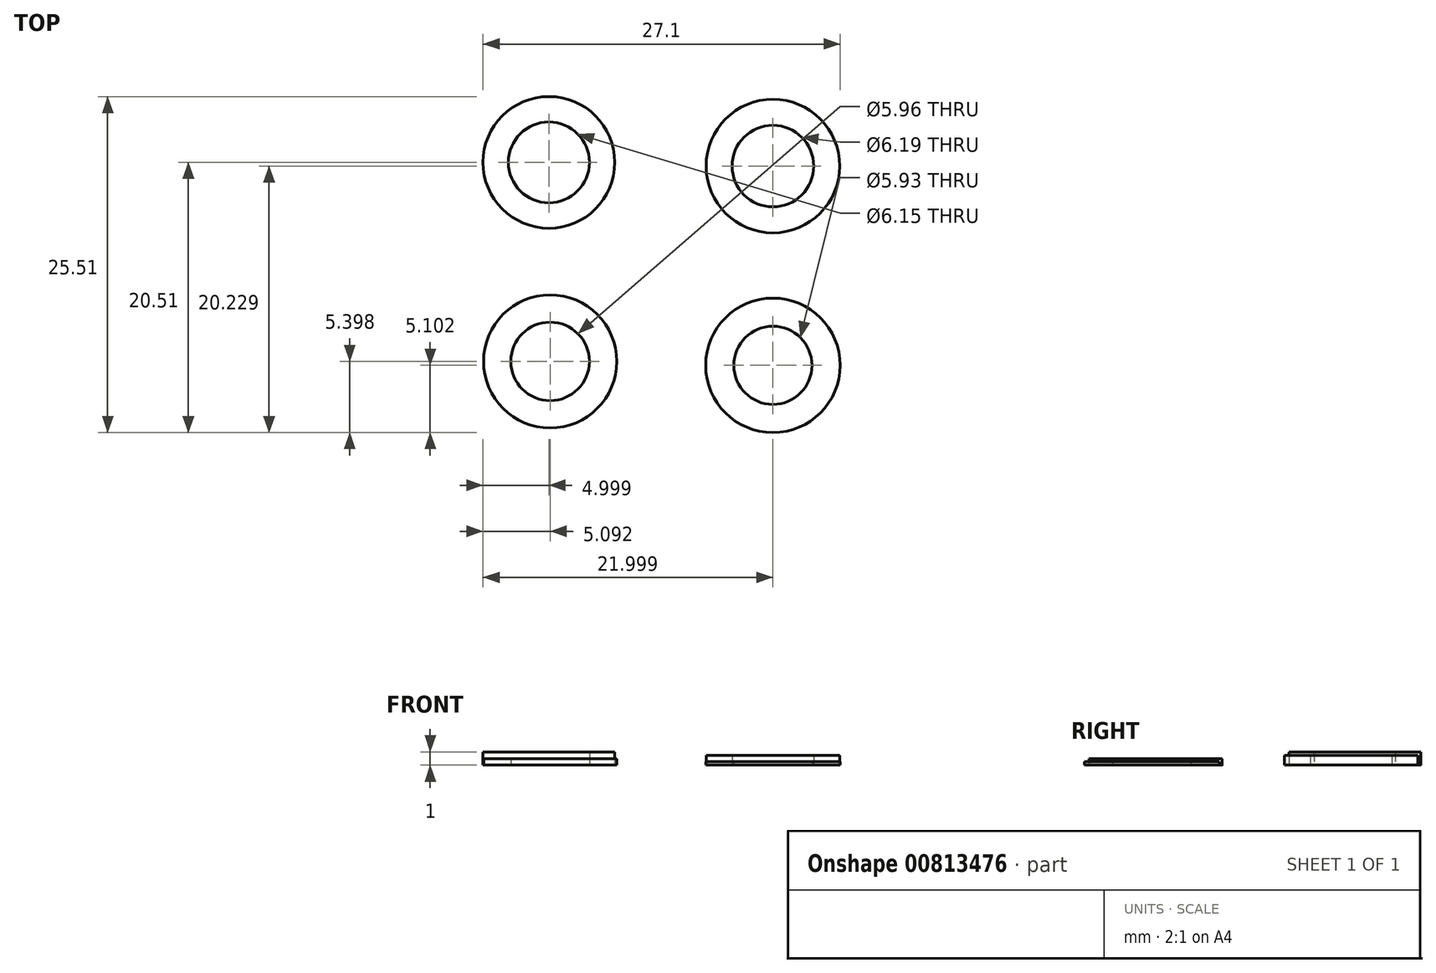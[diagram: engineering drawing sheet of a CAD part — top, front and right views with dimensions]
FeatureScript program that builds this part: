
annotation { "Feature Type Name" : "Feature", "Feature Type Description" : "" }
export const myFeature = defineFeature(function(context is Context, id is Id, definition is map)
    precondition{}
    {
        {
            var Q0;
            Q0=qCreatedBy(makeId("Top.planeOp"),FACE);
            var sketch = newSketch(context, id + "F0", { "sketchPlane" : qUnion([Q0])});
            skCircle(sketch, "E0", {"center": v(-43.62, 36.7) * mm, "radius": 5 * mm});
            skCircle(sketch, "E1", {"center": v(-43.62, 36.7) * mm, "radius": 3.07 * mm});
            skSolve(sketch);
        }
        {
            var Q0;
            Q0=qSketchRegion(id+"F0",true);
            extrude(context, id + "F1", {"entities" : qUnion([Q0]), "depth" : 1 * mm, "offsetDistance" : 25 * mm});
        }
        {
            var Q0;
            Q0=qCreatedBy(makeId("Top.planeOp"),FACE);
            var sketch = newSketch(context, id + "F2", { "sketchPlane" : qUnion([Q0])});
            skCircle(sketch, "E2", {"center": v(-26.62, 36.4) * mm, "radius": 5.07 * mm});
            skCircle(sketch, "E3", {"center": v(-26.62, 36.4) * mm, "radius": 3.1 * mm});
            skSolve(sketch);
        }
        {
            var Q0;
            Q0=qSketchRegion(id+"F2",true);
            extrude(context, id + "F3", {"entities" : qUnion([Q0]), "depth" : .75 * mm, "offsetDistance" : 25 * mm});
        }
        {
            var Q0;
            Q0=qCreatedBy(makeId("Top.planeOp"),FACE);
            var sketch = newSketch(context, id + "F4", { "sketchPlane" : qUnion([Q0])});
            skCircle(sketch, "E4", {"center": v(-43.53, 21.58) * mm, "radius": 5.05 * mm});
            skCircle(sketch, "E5", {"center": v(-43.53, 21.58) * mm, "radius": 2.98 * mm});
            skSolve(sketch);
        }
        {
            var Q0;
            Q0=qSketchRegion(id+"F4",true);
            extrude(context, id + "F5", {"entities" : qUnion([Q0]), "depth" : .5 * mm, "offsetDistance" : 25 * mm});
        }
        {
            var Q0;
            Q0=qCreatedBy(makeId("Top.planeOp"),FACE);
            var sketch = newSketch(context, id + "F6", { "sketchPlane" : qUnion([Q0])});
            skCircle(sketch, "E6", {"center": v(-26.62, 21.28) * mm, "radius": 5.1 * mm});
            skCircle(sketch, "E7", {"center": v(-26.62, 21.28) * mm, "radius": 2.97 * mm});
            skSolve(sketch);
        }
        {
            var Q0;
            Q0=qSketchRegion(id+"F6",true);
            extrude(context, id + "F7", {"entities" : qUnion([Q0]), "depth" : .25 * mm, "offsetDistance" : 25 * mm});
        }
    });
